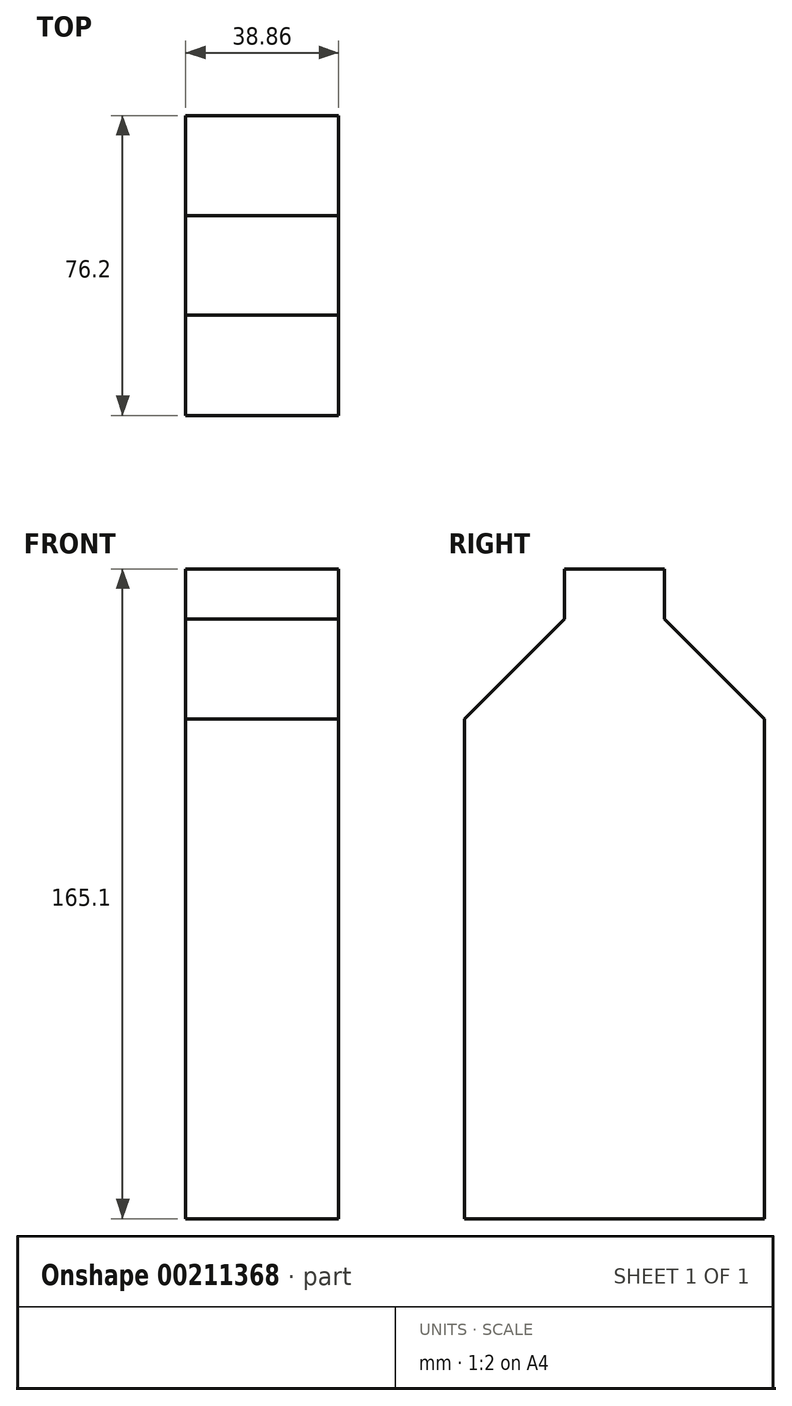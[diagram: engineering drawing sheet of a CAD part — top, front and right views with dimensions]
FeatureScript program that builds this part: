
annotation { "Feature Type Name" : "Feature", "Feature Type Description" : "" }
export const myFeature = defineFeature(function(context is Context, id is Id, definition is map)
    precondition{}
    {
        {
            var Q0;
            Q0=qCreatedBy(makeId("Right.planeOp"),FACE);
            var sketch = newSketch(context, id + "F0", { "sketchPlane" : qUnion([Q0])});
            skLineSegment(sketch, "E0.bottom", {"start": v(38.1, -82.83) * mm, "end": v(-38.1, -82.83) * mm});
            skLineSegment(sketch, "E0.left", {"start": v(38.1, -82.83) * mm, "end": v(38.1, 44.17) * mm});
            skLineSegment(sketch, "E0.right", {"start": v(-38.1, -82.83) * mm, "end": v(-38.1, 44.17) * mm});
            skPoint(sketch, "E0.middle", {"position": v(0, -19.33) * mm});
            skLineSegment(sketch, "E1", {"start": v(38.1, 44.17) * mm, "end": v(12.7, 69.57) * mm});
            skLineSegment(sketch, "E2", {"start": v(12.7, 69.57) * mm, "end": v(12.7, 82.27) * mm});
            skLineSegment(sketch, "E3", {"start": v(12.7, 82.27) * mm, "end": v(0, 82.27) * mm});
            skLineSegment(sketch, "E4.MirrorCS", {"start": v(-12.7, 82.27) * mm, "end": v(0, 82.27) * mm});
            skLineSegment(sketch, "E5.MirrorCS", {"start": v(-12.7, 69.57) * mm, "end": v(-12.7, 82.27) * mm});
            skLineSegment(sketch, "E6.MirrorCS", {"start": v(-38.1, 44.17) * mm, "end": v(-12.7, 69.57) * mm});
            skSolve(sketch);
        }
        {
            var Q0;
            Q0=makeQuery(id+"F0.imprint","IMPRINT",FACE,{"disambiguationData":[TD([[makeQuery(id+"F0.imprint","IMPRINT",EDGE,{"derivedFrom":sQuery(id+"F0.wireOp",EDGE,"E0.bottom")}),-1.0]])]});
            extrude(context, id + "F1", {"entities" : qUnion([Q0]), "depth" : 38.86 * mm});
        }
    });
